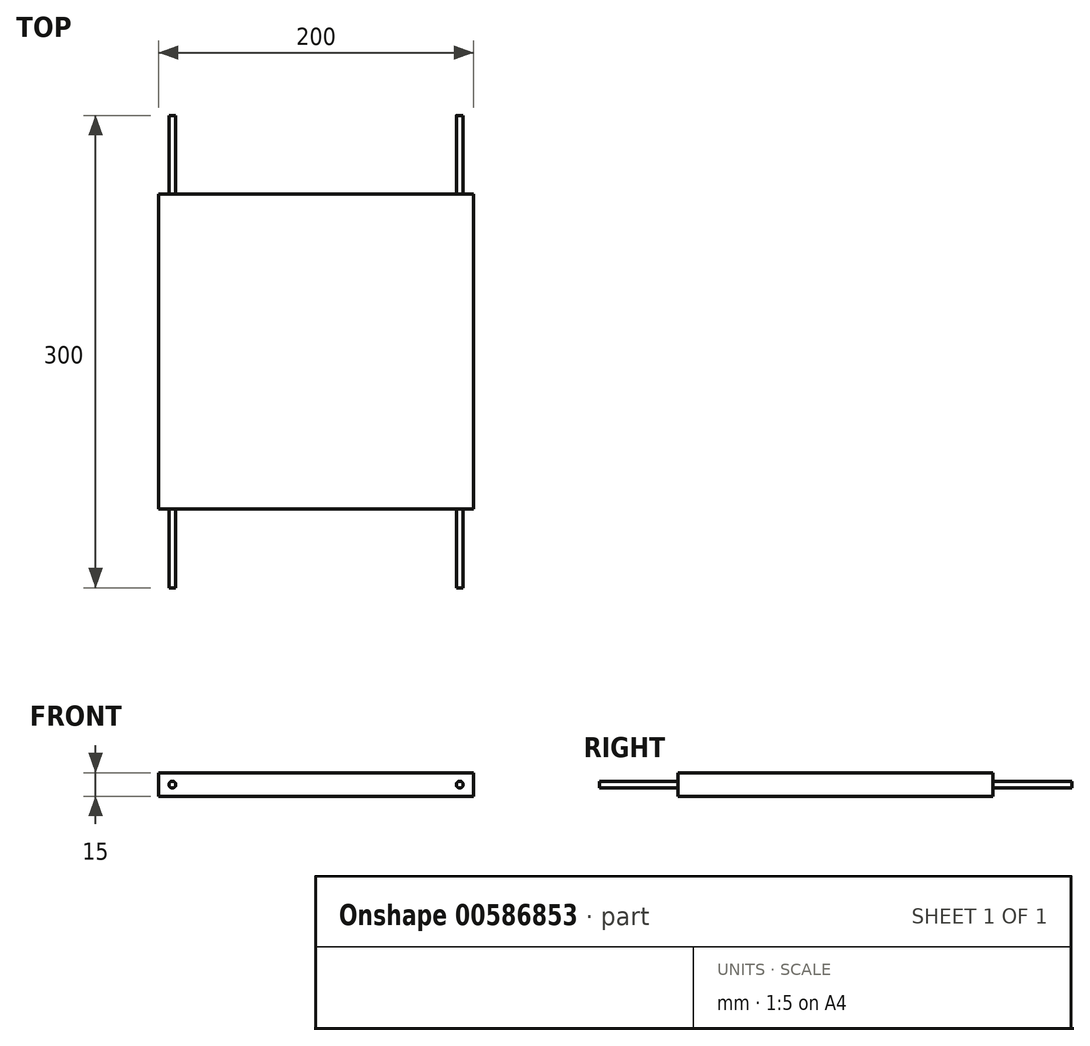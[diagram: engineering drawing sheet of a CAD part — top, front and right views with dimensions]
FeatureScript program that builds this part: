
annotation { "Feature Type Name" : "Feature", "Feature Type Description" : "" }
export const myFeature = defineFeature(function(context is Context, id is Id, definition is map)
    precondition{}
    {
        {
            var Q0;
            Q0=qCreatedBy(makeId("Top.planeOp"),FACE);
            var sketch = newSketch(context, id + "F0", { "sketchPlane" : qUnion([Q0])});
            skLineSegment(sketch, "E0.bottom", {"start": v(100, 100) * mm, "end": v(-100, 100) * mm});
            skLineSegment(sketch, "E0.top", {"start": v(100, -100) * mm, "end": v(-100, -100) * mm});
            skLineSegment(sketch, "E0.left", {"start": v(100, 100) * mm, "end": v(100, -100) * mm});
            skLineSegment(sketch, "E0.right", {"start": v(-100, 100) * mm, "end": v(-100, -100) * mm});
            skPoint(sketch, "E0.middle", {"position": v(0, 0) * mm});
            skSolve(sketch);
        }
        {
            var Q0;
            Q0=makeQuery(id+"F0.imprint","IMPRINT",FACE,{"disambiguationData":[TD([[makeQuery(id+"F0.imprint","IMPRINT",EDGE,{"derivedFrom":sQuery(id+"F0.wireOp",EDGE,"E0.bottom")}),1.0]])]});
            extrude(context, id + "F1", {"entities" : qUnion([Q0]), "depth" : 15 * mm, "offsetDistance" : 25.4 * mm});
        }
        {
            var Q0;
            Q0=makeQuery(id+"F1.opExtrude","SWEPT_FACE",FACE,{"disambiguationData":[OSD([sQuery(id+"F0.wireOp",EDGE,"E0.bottom")])]});
            var sketch = newSketch(context, id + "F2", { "sketchPlane" : qUnion([Q0])});
            skCircle(sketch, "E1", {"center": v(-91.25, 7.5) * mm, "radius": 2.17 * mm});
            skCircle(sketch, "E2", {"center": v(91.25, 7.5) * mm, "radius": 2.17 * mm});
            skSolve(sketch);
        }
        {
            var Q0;
            Q0=makeQuery(id+"F2.imprint","IMPRINT",FACE,{"disambiguationData":[TD([[makeQuery(id+"F2.imprint","IMPRINT",EDGE,{"derivedFrom":sQuery(id+"F2.wireOp",EDGE,"E1")}),1.0]])]});
            var Q1;
            Q1=makeQuery(id+"F2.imprint","IMPRINT",FACE,{"disambiguationData":[TD([[makeQuery(id+"F2.imprint","IMPRINT",EDGE,{"derivedFrom":sQuery(id+"F2.wireOp",EDGE,"E2")}),1.0]])]});
            var Q2;
            Q2=sQuery(id+"F2.wireOp",EDGE,"E1");
            var Q3;
            Q3=sQuery(id+"F2.wireOp",EDGE,"E2");
            extrude(context, id + "F3", {"entities" : qUnion([Q0, Q1]), "operationType" : NewBodyOperationType.ADD, "surfaceEntities" : qUnion([Q2, Q3]), "depth" : 50 * mm, "offsetDistance" : 25.4 * mm});
        }
        {
            var Q0;
            Q0=makeQuery(id+"F1.opExtrude","SWEPT_FACE",FACE,{"disambiguationData":[OSD([sQuery(id+"F0.wireOp",EDGE,"E0.top")])]});
            var sketch = newSketch(context, id + "F4", { "sketchPlane" : qUnion([Q0])});
            skCircle(sketch, "E3", {"center": v(-91.25, 7.5) * mm, "radius": 2.17 * mm});
            skCircle(sketch, "E4", {"center": v(91.25, 7.5) * mm, "radius": 2.17 * mm});
            skSolve(sketch);
        }
        {
            var Q0;
            Q0=makeQuery(id+"F4.imprint","IMPRINT",FACE,{"disambiguationData":[TD([[makeQuery(id+"F4.imprint","IMPRINT",EDGE,{"derivedFrom":sQuery(id+"F4.wireOp",EDGE,"E3")}),1.0]])]});
            var Q1;
            Q1=makeQuery(id+"F4.imprint","IMPRINT",FACE,{"disambiguationData":[TD([[makeQuery(id+"F4.imprint","IMPRINT",EDGE,{"derivedFrom":sQuery(id+"F4.wireOp",EDGE,"E4")}),1.0]])]});
            var Q2;
            Q2=sQuery(id+"F4.wireOp",EDGE,"E3");
            var Q3;
            Q3=sQuery(id+"F4.wireOp",EDGE,"E4");
            extrude(context, id + "F5", {"entities" : qUnion([Q0, Q1]), "operationType" : NewBodyOperationType.ADD, "surfaceEntities" : qUnion([Q2, Q3]), "depth" : 50 * mm, "offsetDistance" : 25.4 * mm});
        }
    });
